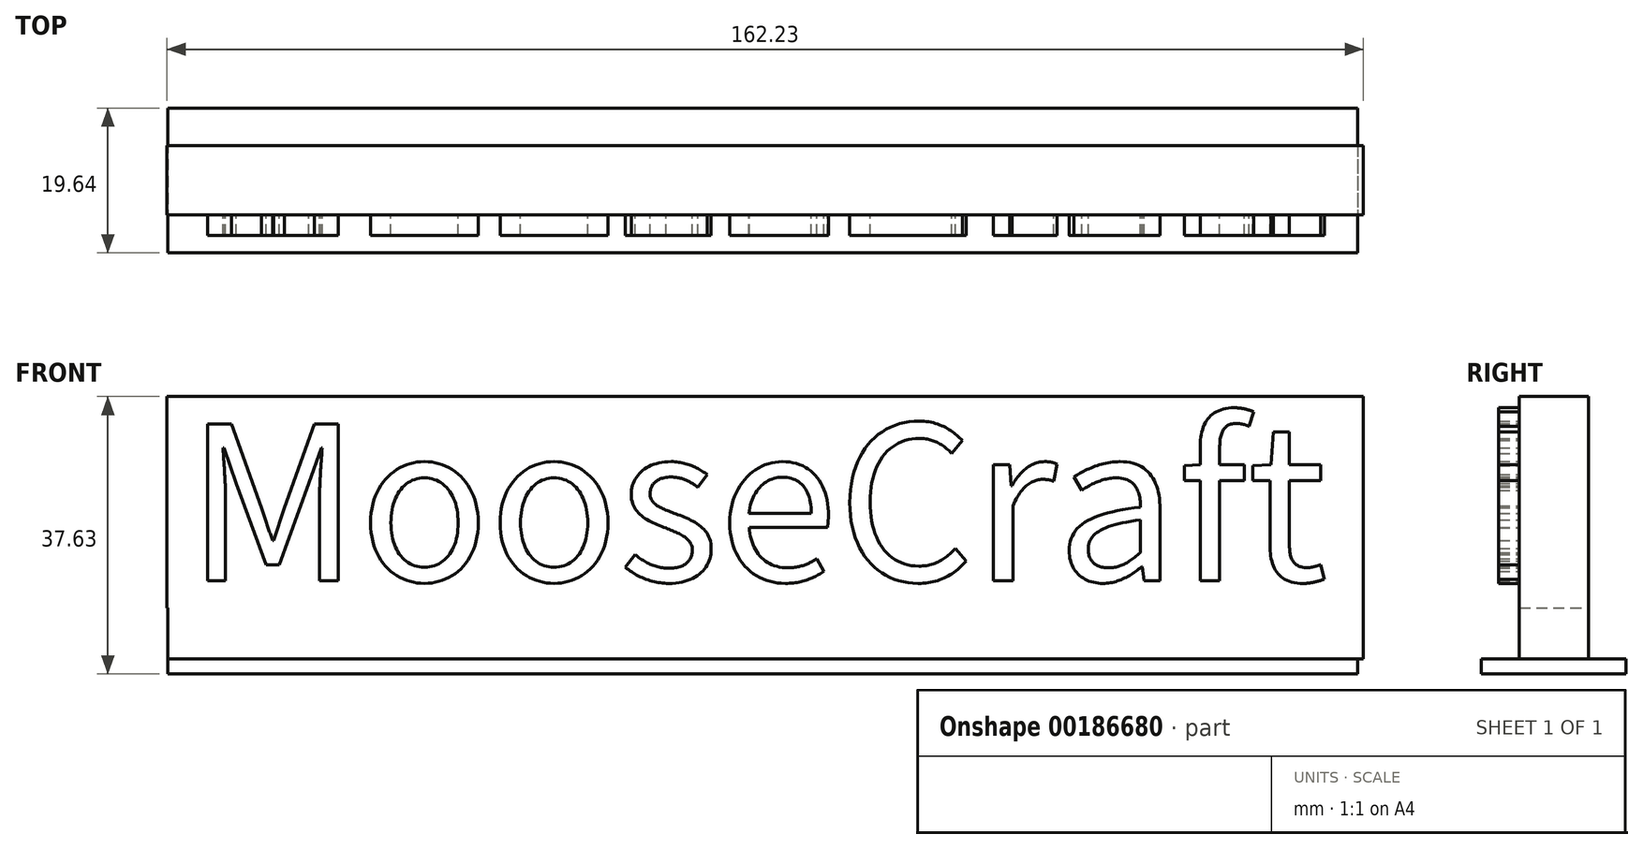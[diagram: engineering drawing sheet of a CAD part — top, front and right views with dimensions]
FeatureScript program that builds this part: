
annotation { "Feature Type Name" : "Feature", "Feature Type Description" : "" }
export const myFeature = defineFeature(function(context is Context, id is Id, definition is map)
    precondition{}
    {
        {
            var Q0;
            Q0=qCreatedBy(makeId("Front.planeOp"),FACE);
            var sketch = newSketch(context, id + "F0", { "sketchPlane" : qUnion([Q0])});
            skLineSegment(sketch, "E0.bottom", {"start": v(75.7, 14.33) * mm, "end": v(-75.7, 14.33) * mm});
            skLineSegment(sketch, "E0.top", {"start": v(-75.6, -14.33) * mm, "end": v(-75.7, -14.33) * mm});
            skLineSegment(sketch, "E0.right", {"start": v(-75.7, 14.33) * mm, "end": v(-75.7, -14.33) * mm});
            skPoint(sketch, "E0.middle", {"position": v(0, 0) * mm});
            skLineSegment(sketch, "E1.bottom", {"start": v(-75.7, 14.33) * mm, "end": v(86.53, 14.33) * mm});
            skLineSegment(sketch, "E1.left", {"start": v(-75.7, -14.33) * mm, "end": v(-75.7, -14.54) * mm});
            skLineSegment(sketch, "E1.right", {"start": v(86.53, 14.33) * mm, "end": v(86.53, -14.54) * mm});
            skLineSegment(sketch, "E2.bottom", {"start": v(86.53, 14.33) * mm, "end": v(-75.6, 14.33) * mm});
            skLineSegment(sketch, "E2.top", {"start": v(86.53, -21.27) * mm, "end": v(-75.6, -21.27) * mm});
            skLineSegment(sketch, "E2.left", {"start": v(86.53, 14.33) * mm, "end": v(86.53, -21.27) * mm});
            skLineSegment(sketch, "E2.right", {"start": v(-75.6, -14.33) * mm, "end": v(-75.6, -21.27) * mm});
            skPoint(sketch, "E3.start.orphan", {"position": v(75.7, -14.33) * mm});
            skSolve(sketch);
        }
        {
            var Q0;
            Q0 = qSketchRegion(id + "F0", true);
            extrude(context, id + "F1", {"entities" : qUnion([Q0]), "depth" : 9.4 * mm});
        }
        {
            var Q0;
            Q0=makeQuery(id+"F1.opExtrude","CAP_FACE",FACE,{"disambiguationData":[OSD([sQuery(id+"F0.wireOp",EDGE,"E0.bottom"),sQuery(id+"F0.wireOp",EDGE,"E0.top"),sQuery(id+"F0.wireOp",EDGE,"E0.left"),sQuery(id+"F0.wireOp",EDGE,"E0.right")])],"isStart":false});
            var sketch = newSketch(context, id + "F2", { "sketchPlane" : qUnion([Q0])});
            skText(sketch, "E4", { "text": "MooseCraft", "fontName": "NotoSansCJKjp-Regular.otf"});
            const initialGuessF2  = {"E4": [-0.07312, -0.01065, 1, 0, 0.02088]};
            skSetInitialGuess(sketch, initialGuessF2);
            skSolve(sketch);
        }
        {
            var Q0;
            Q0 = qSketchRegion(id + "F2", true);
            extrude(context, id + "F3", {"entities" : qUnion([Q0]), "operationType" : NewBodyOperationType.ADD, "depth" : 2.8 * mm});
        }
        {
            var Q0;
            Q0=makeQuery(id+"F1.opExtrude","SWEPT_FACE",FACE,{"disambiguationData":[OSD([sQuery(id+"F0.wireOp",EDGE,"E2.top")])]});
            var sketch = newSketch(context, id + "F4", { "sketchPlane" : qUnion([Q0])});
            skLineSegment(sketch, "E5.bottom", {"start": v(-75.6, 9.4) * mm, "end": v(86.36, 9.4) * mm});
            skLineSegment(sketch, "E5.top", {"start": v(-75.6, -5.07) * mm, "end": v(86.36, -5.07) * mm});
            skLineSegment(sketch, "E5.left", {"start": v(-75.6, 9.4) * mm, "end": v(-75.6, -5.07) * mm});
            skPoint(sketch, "E6.right.end.orphan", {"position": v(86.36, 23.93) * mm});
            skLineSegment(sketch, "E7.bottom", {"start": v(-75.6, 0) * mm, "end": v(85.78, 0) * mm});
            skLineSegment(sketch, "E7.top", {"start": v(-75.6, 14.57) * mm, "end": v(85.78, 14.57) * mm});
            skLineSegment(sketch, "E7.left", {"start": v(-75.6, 0) * mm, "end": v(-75.6, 14.57) * mm});
            skLineSegment(sketch, "E7.right", {"start": v(85.78, 0) * mm, "end": v(85.78, 14.57) * mm});
            skLineSegment(sketch, "E8.bottom", {"start": v(85.78, 0) * mm, "end": v(86.36, 0) * mm});
            skLineSegment(sketch, "E8.top", {"start": v(85.78, -5.07) * mm, "end": v(86.36, -5.07) * mm});
            skLineSegment(sketch, "E8.left", {"start": v(85.78, 0) * mm, "end": v(85.78, -5.07) * mm});
            skSolve(sketch);
        }
        {
            var Q0;
            Q0 = qSketchRegion(id + "F4", true);
            extrude(context, id + "F5", {"entities" : qUnion([Q0]), "operationType" : NewBodyOperationType.ADD, "depth" : 2.03 * mm});
        }
    });
